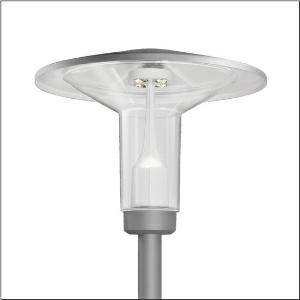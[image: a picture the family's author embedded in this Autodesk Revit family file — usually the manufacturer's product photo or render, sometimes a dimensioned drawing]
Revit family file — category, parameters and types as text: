
# Revit family: laterne_iq___st1_2a_5xa5255kf14h_a0c9
name_source: partatom
category: Lighting Fixtures
units: mm (PartAtom-declared; Revit-internal decimal feet)

## family parameters
Cut with Voids When Loaded = No
Host = Face
Light Source = No
Part Type = Normal
Room Calculation Point = No
Round Connector Dimension = Use Diameter
Shared = No

## types (1)
- --- (1 x LED, 1540 lm, 10 W, 4000K)
    Apparent Load = 10 VA
    CIE Flux Codes = 25 63 94 98 100
    Color Rendering = 70
    Color Temperature = 4000K
    Default Elevation = 1800 mm
    Description = Lantern iQ, mast luminaire, Module 540 iQ-SR, primary light control with 3 zone facetted reflector, of plastic, silver coated, highly specular, structured, primary optical cover: cover, of PMMA, transparent, light distribution: ST1.2a, light emission: direct distribution, primary light characteristic: asymmetric, installation type: post-top, LED, High Power LED, rated luminous flux: 1.540lm, luminous efficacy: 154lm/W, light colour: 740, colour temperature: 4000K, control gear: ECG iQ, control: presetting dimming logarithmic, Street-Remote, Auto-Match, Temp-Guard, Lumen-Switch, Night-Set, Smart-Wire, Light-Fading, Desk-Remote (wireless, voltage-free reading and setting of iQ features in the workshop via application-optimized NFC function/RFID function), optimised constant luminous flux control (CLO 2.0), with terminal, 6-pole, max. 2.5mm², mains connection: 230..240V, AC, 50/60Hz, start of lifetime: 10W, end of service life: 10W, reduction: 5W, luminaire housing, upper part, of glass-fibre reinforced polyester, coated, Siteco® metallic grey (DB 702S), diameter: 750mm, height: 583mm, spigot size: d x l = 76 x 70mm (post-top) | with reducer (optional accessory) 60 x 70mm, post-top mast mounting element, of diecast aluminium, coated, Siteco® metallic grey (DB 702S), Module 540 iQ-SR, traffic white (RAL 9016), equipment: standard, protection rating (complete): IP65, insulation class (complete): insulation class II (safety insulation), certification: CE, ENEC, VDE, packaging unit: 1 piece

Light Distribution: ST1.2a
    Height = 583 mm
    Lamp = 1 x LED
    Lamp Light Flux = 1540 lm
    Lamp Power = 10 W
    Lamp count = 1
    Length = 750 mm
    Luminous efficacy = 154 lm/W
    Manufacturer = Siteco
    ModVariant = No
    Model = 5XA5255KF14H
    Number of Poles = 1
    OnlyDefault = Yes
    Power Factor = 1
    Product Name = Laterne iQ | ST1.2a
    Product group = mast luminaire | pylon top
    ProductGroupID = 6100
    Protection Class = Protection class II
    Protection Degree = IP 65
    RLX_Detail_Level = 1
    RLX_Emergency_Light_Flux = 0 lm
    RLX_Emergency_Type = 0
    RLX_Emergency_Type_DB = No
    RlxData = <blob elided: 107089 chars, md5=0ef17860>
    Socket = socket
    Standby Power = 0 W
    System Light Flux = 1540 lm
    System Power = 10 W
    Type Comments = factory setting: luminous flux: 100 % | dim-lin: 254 | 401 mA
    Type Image = l_1006050.jpg
    URL = http://relux.com
    VarID = @adj_092927
    Voltage = 0 V
    Weight = 0.00 kg
    Width = 0 mm  [stored 0 ft]

note: [stored X ft] marks values corroborated as IEEE doubles in the binary element streams (Revit-internal decimal feet)

## geometry (parser evidence)
native form markers: Blend x4, Sweep x10
no freeform markers — native parametric forms only
